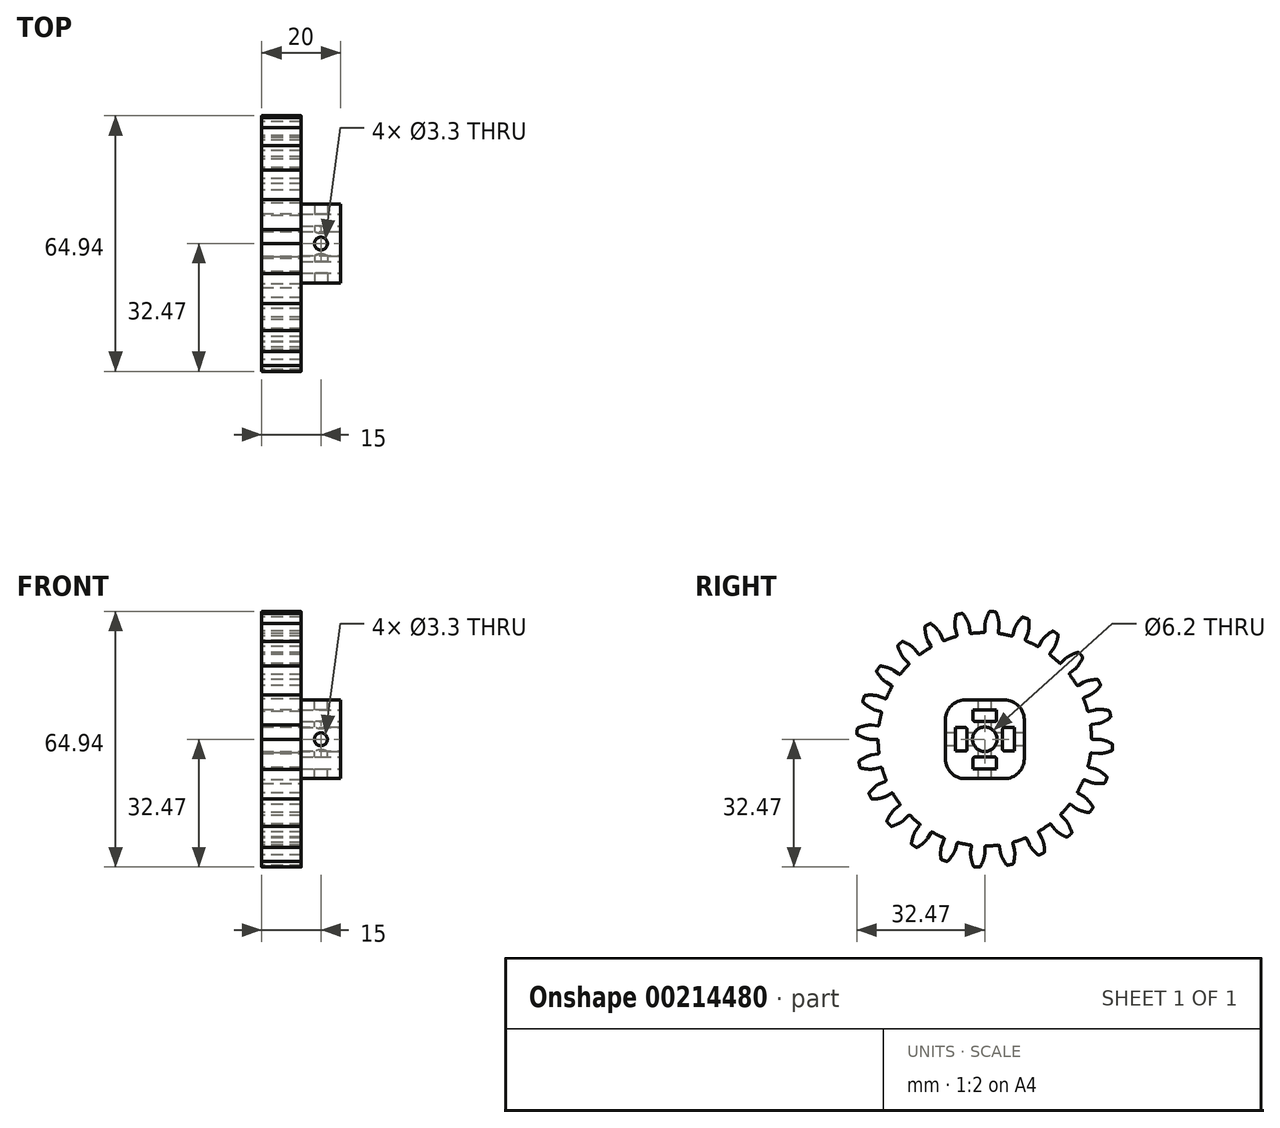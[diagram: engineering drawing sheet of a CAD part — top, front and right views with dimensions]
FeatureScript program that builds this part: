
annotation { "Feature Type Name" : "Feature", "Feature Type Description" : "" }
export const myFeature = defineFeature(function(context is Context, id is Id, definition is map)
    precondition{}
    {
        {
            assignVariable(context, id + "F0", {"name" : "NumberTeeth", "anyValue" : 24});
        }
        {
            assignVariable(context, id + "F1", {"name" : "GearThickness", "anyValue" : 10});
        }
        {
            var Q0;
            Q0=qCreatedBy(makeId("Right.planeOp"),FACE);
            var sketch = newSketch(context, id + "F2", { "sketchPlane" : qUnion([Q0])});
            skCircle(sketch, "E0", {"center": v(0, 0) * mm, "radius": 27.1 * mm});
            skCircle(sketch, "E1", {"center": v(0, 0) * mm, "radius": 29.04 * mm, "construction": true});
            skCircle(sketch, "E2", {"center": v(0, 0) * mm, "radius": 30 * mm, "construction": true});
            skCircle(sketch, "E3", {"center": v(0, 0) * mm, "radius": 32.5 * mm});
            skLineSegment(sketch, "E4", {"start": v(0, 0) * mm, "end": v(-29.04, 0) * mm, "construction": true});
            skLineSegment(sketch, "E5.1.0", {"start": v(0, 0) * mm, "end": v(-29, 1.45) * mm, "construction": true});
            skLineSegment(sketch, "E5.2.0", {"start": v(0, 0) * mm, "end": v(-28.9, 2.9) * mm, "construction": true});
            skLineSegment(sketch, "E5.3.0", {"start": v(0, 0) * mm, "end": v(-28.72, 4.34) * mm, "construction": true});
            skLineSegment(sketch, "E5.4.0", {"start": v(0, 0) * mm, "end": v(-28.47, 5.77) * mm, "construction": true});
            skLineSegment(sketch, "E5.5.0", {"start": v(0, 0) * mm, "end": v(-28.14, 7.19) * mm, "construction": true});
            skLineSegment(sketch, "E5.6.0", {"start": v(0, 0) * mm, "end": v(-27.75, 8.58) * mm, "construction": true});
            skLineSegment(sketch, "E5.7.0", {"start": v(0, 0) * mm, "end": v(-27.28, 9.96) * mm, "construction": true});
            skLineSegment(sketch, "E5.8.0", {"start": v(0, 0) * mm, "end": v(-26.75, 11.31) * mm, "construction": true});
            skLineSegment(sketch, "E5.9.0", {"start": v(0, 0) * mm, "end": v(-26.15, 12.63) * mm, "construction": true});
            skLineSegment(sketch, "E5.10.0", {"start": v(0, 0) * mm, "end": v(-25.49, 13.92) * mm, "construction": true});
            skLineSegment(sketch, "E5.11.0", {"start": v(0, 0) * mm, "end": v(-24.76, 15.18) * mm, "construction": true});
            skLineSegment(sketch, "E5.12.0", {"start": v(0, 0) * mm, "end": v(-23.97, 16.4) * mm, "construction": true});
            skLineSegment(sketch, "E5.13.0", {"start": v(0, 0) * mm, "end": v(-23.12, 17.58) * mm, "construction": true});
            skLineSegment(sketch, "E5.14.0", {"start": v(0, 0) * mm, "end": v(-22.21, 18.71) * mm, "construction": true});
            skLineSegment(sketch, "E5.anchor2", {"start": v(0, 0) * mm, "end": v(-22.21, 18.71) * mm, "construction": true});
            skLineSegment(sketch, "E6", {"start": v(-29, 1.45) * mm, "end": v(-29.08, 0) * mm, "construction": true});
            skLineSegment(sketch, "E7", {"start": v(-28.9, 2.9) * mm, "end": v(-29.19, 0) * mm, "construction": true});
            skLineSegment(sketch, "E8", {"start": v(-28.72, 4.34) * mm, "end": v(-29.37, 0.03) * mm, "construction": true});
            skLineSegment(sketch, "E9", {"start": v(-28.14, 7.19) * mm, "end": v(-29.94, 0.15) * mm, "construction": true});
            skLineSegment(sketch, "E10", {"start": v(-27.75, 8.58) * mm, "end": v(-30.32, 0.26) * mm, "construction": true});
            skLineSegment(sketch, "E11", {"start": v(-27.28, 9.96) * mm, "end": v(-30.77, 0.41) * mm, "construction": true});
            skLineSegment(sketch, "E12", {"start": v(-26.75, 11.31) * mm, "end": v(-31.28, 0.6) * mm, "construction": true});
            skLineSegment(sketch, "E13", {"start": v(-26.15, 12.63) * mm, "end": v(-31.84, 0.86) * mm, "construction": true});
            skLineSegment(sketch, "E14", {"start": v(-25.49, 13.92) * mm, "end": v(-32.45, 1.18) * mm, "construction": true});
            skLineSegment(sketch, "E15", {"start": v(-24.76, 15.18) * mm, "end": v(-33.11, 1.56) * mm, "construction": true});
            skLineSegment(sketch, "E16", {"start": v(-28.47, 5.77) * mm, "end": v(-29.62, 0.08) * mm, "construction": true});
            skLineSegment(sketch, "E17", {"start": v(-23.97, 16.4) * mm, "end": v(-33.81, 2.02) * mm, "construction": true});
            skLineSegment(sketch, "E18", {"start": v(-23.12, 17.58) * mm, "end": v(-34.55, 2.55) * mm, "construction": true});
            skLineSegment(sketch, "E19", {"start": v(-22.21, 18.71) * mm, "end": v(-35.31, 3.16) * mm, "construction": true});
            skLineSegment(sketch, "E20", {"start": v(0, 0) * mm, "end": v(-28.99, 1.8) * mm, "construction": true});
            skLineSegment(sketch, "E21", {"start": v(-27.1, 0) * mm, "end": v(-29.04, 0) * mm});
            skLineSegment(sketch, "E22.MirrorCS", {"start": v(-26.9, 3.37) * mm, "end": v(-28.82, 3.61) * mm});
            skLineSegment(sketch, "E23", {"start": v(-29.3, -1.9) * mm, "end": v(-35.31, 3.16) * mm, "construction": true});
            skFitSpline(sketch, "E24", {"points": [v(-35.31, 3.16) * mm, v(-34.55, 2.55) * mm, v(-33.81, 2.02) * mm, v(-33.11, 1.56) * mm, v(-32.45, 1.18) * mm, v(-31.84, 0.86) * mm, v(-31.28, 0.6) * mm, v(-30.77, 0.41) * mm, v(-30.32, 0.26) * mm, v(-29.94, 0.15) * mm, v(-29.62, 0.08) * mm, v(-29.37, 0.03) * mm, v(-29.19, 0) * mm, v(-29.08, 0) * mm, v(-29.04, 0) * mm], "startDerivative": vector(7.75, -6.31) * mm, "endDerivative": vector(1.01, 0) * mm});
            skFitSpline(sketch, "E25.MirrorCS", {"points": [v(-35.43, 1.25) * mm, v(-34.6, 1.77) * mm, v(-33.8, 2.2) * mm, v(-33.05, 2.57) * mm, v(-32.35, 2.86) * mm, v(-31.7, 3.1) * mm, v(-31.1, 3.28) * mm, v(-30.58, 3.42) * mm, v(-30.12, 3.51) * mm, v(-29.72, 3.57) * mm, v(-29.4, 3.6) * mm, v(-29.15, 3.62) * mm, v(-28.96, 3.62) * mm, v(-28.86, 3.61) * mm, v(-28.82, 3.61) * mm], "startDerivative": vector(8.48, 5.3) * mm, "endDerivative": vector(1, -0.13) * mm});
            skSolve(sketch);
        }
        {
            var Q0;
            {var subQ0=sQuery(id+"F2.wireOp",EDGE,"E0");var subQ27=makeQuery(id+"F2.imprint","INTERSECT",VERTEX,{"derivedFrom":[subQ0,sQuery(id+"F2.wireOp",EDGE,"10ea1024-8cf5-41f5-a75f-a634b86921f3.10.0")]});Q0=makeQuery(id+"F2.imprint","IMPRINT",FACE,{"disambiguationData":[TD([[makeQuery(id+"F2.imprint","IMPRINT",EDGE,{"disambiguationData":[TD([[subQ27,-1.0]])],"derivedFrom":subQ0}),1.0]])]});}
            var Q1;
            {var subQ0=sQuery(id+"F2.wireOp",EDGE,"10ea1024-8cf5-41f5-a75f-a634b86921f3.1.0");Q1=makeQuery(id+"F2.imprint","IMPRINT",FACE,{"disambiguationData":[TD([[makeQuery(id+"F2.imprint","IMPRINT",EDGE,{"derivedFrom":subQ0}),-1.0]])]});}
            var Q2;
            {var subQ7=sQuery(id+"F2.wireOp",EDGE,"10ea1024-8cf5-41f5-a75f-a634b86921f3.2.0");Q2=makeQuery(id+"F2.imprint","IMPRINT",FACE,{"disambiguationData":[TD([[makeQuery(id+"F2.imprint","IMPRINT",EDGE,{"derivedFrom":subQ7}),-1.0]])]});}
            var Q3;
            {var subQ8=sQuery(id+"F2.wireOp",EDGE,"10ea1024-8cf5-41f5-a75f-a634b86921f3.3.0");Q3=makeQuery(id+"F2.imprint","IMPRINT",FACE,{"disambiguationData":[TD([[makeQuery(id+"F2.imprint","IMPRINT",EDGE,{"derivedFrom":subQ8}),-1.0]])]});}
            var Q4;
            {var subQ2=sQuery(id+"F2.wireOp",EDGE,"10ea1024-8cf5-41f5-a75f-a634b86921f3.4.0");Q4=makeQuery(id+"F2.imprint","IMPRINT",FACE,{"disambiguationData":[TD([[makeQuery(id+"F2.imprint","IMPRINT",EDGE,{"derivedFrom":subQ2}),-1.0]])]});}
            var Q5;
            {var subQ8=sQuery(id+"F2.wireOp",EDGE,"10ea1024-8cf5-41f5-a75f-a634b86921f3.5.0");Q5=makeQuery(id+"F2.imprint","IMPRINT",FACE,{"disambiguationData":[TD([[makeQuery(id+"F2.imprint","IMPRINT",EDGE,{"derivedFrom":subQ8}),-1.0]])]});}
            var Q6;
            {var subQ3=sQuery(id+"F2.wireOp",EDGE,"10ea1024-8cf5-41f5-a75f-a634b86921f3.6.0");Q6=makeQuery(id+"F2.imprint","IMPRINT",FACE,{"disambiguationData":[TD([[makeQuery(id+"F2.imprint","IMPRINT",EDGE,{"derivedFrom":subQ3}),-1.0]])]});}
            var Q7;
            {var subQ0=sQuery(id+"F2.wireOp",EDGE,"10ea1024-8cf5-41f5-a75f-a634b86921f3.7.0");Q7=makeQuery(id+"F2.imprint","IMPRINT",FACE,{"disambiguationData":[TD([[makeQuery(id+"F2.imprint","IMPRINT",EDGE,{"derivedFrom":subQ0}),-1.0]])]});}
            var Q8;
            {var subQ5=sQuery(id+"F2.wireOp",EDGE,"10ea1024-8cf5-41f5-a75f-a634b86921f3.8.0");Q8=makeQuery(id+"F2.imprint","IMPRINT",FACE,{"disambiguationData":[TD([[makeQuery(id+"F2.imprint","IMPRINT",EDGE,{"derivedFrom":subQ5}),-1.0]])]});}
            var Q9;
            {var subQ1=sQuery(id+"F2.wireOp",EDGE,"10ea1024-8cf5-41f5-a75f-a634b86921f3.9.0");Q9=makeQuery(id+"F2.imprint","IMPRINT",FACE,{"disambiguationData":[TD([[makeQuery(id+"F2.imprint","IMPRINT",EDGE,{"derivedFrom":subQ1}),-1.0]])]});}
            var Q10;
            {var subQ5=sQuery(id+"F2.wireOp",EDGE,"10ea1024-8cf5-41f5-a75f-a634b86921f3.10.0");Q10=makeQuery(id+"F2.imprint","IMPRINT",FACE,{"disambiguationData":[TD([[makeQuery(id+"F2.imprint","IMPRINT",EDGE,{"derivedFrom":subQ5}),-1.0]])]});}
            var Q11;
            {var subQ8=sQuery(id+"F2.wireOp",EDGE,"10ea1024-8cf5-41f5-a75f-a634b86921f3.11.0");Q11=makeQuery(id+"F2.imprint","IMPRINT",FACE,{"disambiguationData":[TD([[makeQuery(id+"F2.imprint","IMPRINT",EDGE,{"derivedFrom":subQ8}),-1.0]])]});}
            var Q12;
            {var subQ2=sQuery(id+"F2.wireOp",EDGE,"10ea1024-8cf5-41f5-a75f-a634b86921f3.12.0");Q12=makeQuery(id+"F2.imprint","IMPRINT",FACE,{"disambiguationData":[TD([[makeQuery(id+"F2.imprint","IMPRINT",EDGE,{"derivedFrom":subQ2}),-1.0]])]});}
            var Q13;
            {var subQ3=sQuery(id+"F2.wireOp",EDGE,"10ea1024-8cf5-41f5-a75f-a634b86921f3.13.0");Q13=makeQuery(id+"F2.imprint","IMPRINT",FACE,{"disambiguationData":[TD([[makeQuery(id+"F2.imprint","IMPRINT",EDGE,{"derivedFrom":subQ3}),-1.0]])]});}
            var Q14;
            {var subQ0=sQuery(id+"F2.wireOp",EDGE,"10ea1024-8cf5-41f5-a75f-a634b86921f3.14.0");Q14=makeQuery(id+"F2.imprint","IMPRINT",FACE,{"disambiguationData":[TD([[makeQuery(id+"F2.imprint","IMPRINT",EDGE,{"derivedFrom":subQ0}),-1.0]])]});}
            var Q15;
            {var subQ6=sQuery(id+"F2.wireOp",EDGE,"10ea1024-8cf5-41f5-a75f-a634b86921f3.15.0");Q15=makeQuery(id+"F2.imprint","IMPRINT",FACE,{"disambiguationData":[TD([[makeQuery(id+"F2.imprint","IMPRINT",EDGE,{"derivedFrom":subQ6}),-1.0]])]});}
            var Q16;
            {var subQ5=sQuery(id+"F2.wireOp",EDGE,"10ea1024-8cf5-41f5-a75f-a634b86921f3.16.0");Q16=makeQuery(id+"F2.imprint","IMPRINT",FACE,{"disambiguationData":[TD([[makeQuery(id+"F2.imprint","IMPRINT",EDGE,{"derivedFrom":subQ5}),-1.0]])]});}
            var Q17;
            {var subQ7=sQuery(id+"F2.wireOp",EDGE,"10ea1024-8cf5-41f5-a75f-a634b86921f3.17.0");Q17=makeQuery(id+"F2.imprint","IMPRINT",FACE,{"disambiguationData":[TD([[makeQuery(id+"F2.imprint","IMPRINT",EDGE,{"derivedFrom":subQ7}),-1.0]])]});}
            var Q18;
            {var subQ5=sQuery(id+"F2.wireOp",EDGE,"10ea1024-8cf5-41f5-a75f-a634b86921f3.18.0");Q18=makeQuery(id+"F2.imprint","IMPRINT",FACE,{"disambiguationData":[TD([[makeQuery(id+"F2.imprint","IMPRINT",EDGE,{"derivedFrom":subQ5}),-1.0]])]});}
            var Q19;
            {var subQ8=sQuery(id+"F2.wireOp",EDGE,"10ea1024-8cf5-41f5-a75f-a634b86921f3.19.0");Q19=makeQuery(id+"F2.imprint","IMPRINT",FACE,{"disambiguationData":[TD([[makeQuery(id+"F2.imprint","IMPRINT",EDGE,{"derivedFrom":subQ8}),-1.0]])]});}
            var Q20;
            {var subQ8=sQuery(id+"F2.wireOp",EDGE,"E21");Q20=makeQuery(id+"F2.imprint","IMPRINT",FACE,{"disambiguationData":[TD([[makeQuery(id+"F2.imprint","IMPRINT",EDGE,{"derivedFrom":subQ8}),-1.0]])]});}
            extrude(context, id + "F3", {"entities" : qUnion([Q0, Q1, Q2, Q3, Q4, Q5, Q6, Q7, Q8, Q9, Q10, Q11, Q12, Q13, Q14, Q15, Q16, Q17, Q18, Q19, Q20]), "depth" : (getVariable(context, 'GearThickness')) * mm});
        }
        {
            var Q0;
            Q0=makeQuery(id+"F3.opExtrude","SWEPT_EDGE",EDGE,{"disambiguationData":[OSD([sQuery(id+"F2.wireOp",EDGE,"E0"),sQuery(id+"F2.wireOp",EDGE,"E22.MirrorCS")])]});
            var Q1;
            Q1=makeQuery(id+"F3.opExtrude","SWEPT_EDGE",EDGE,{"disambiguationData":[OSD([sQuery(id+"F2.wireOp",EDGE,"E3"),sQuery(id+"F2.wireOp",EDGE,"E25.MirrorCS")])]});
            var Q2;
            Q2=makeQuery(id+"F3.opExtrude","SWEPT_EDGE",EDGE,{"disambiguationData":[OSD([sQuery(id+"F2.wireOp",EDGE,"E3"),sQuery(id+"F2.wireOp",EDGE,"E24")])]});
            var Q3;
            Q3=makeQuery(id+"F3.opExtrude","SWEPT_EDGE",EDGE,{"disambiguationData":[OSD([sQuery(id+"F2.wireOp",EDGE,"E0"),sQuery(id+"F2.wireOp",EDGE,"E21")])]});
            fillet(context, id + "F4", {"entities" : qUnion([Q0, Q1, Q2, Q3]), "radius" : 0.3 * mm, "tangentPropagation" : true, "allowEdgeOverflow" : false});
        }
        {
            var Q0;
            Q0=makeQuery(id+"F3.opExtrude","SWEPT_FACE",FACE,{"disambiguationData":[OSD([sQuery(id+"F2.wireOp",EDGE,"E22.MirrorCS")])]});
            var Q1;
            Q1=makeQuery(id+"F3.opExtrude","SWEPT_FACE",FACE,{"disambiguationData":[OSD([sQuery(id+"F2.wireOp",EDGE,"E25.MirrorCS")])]});
            var Q2;
            Q2=makeQuery(id+"F3.opExtrude","SWEPT_FACE",FACE,{"disambiguationData":[OSD([sQuery(id+"F2.wireOp",EDGE,"E3")])]});
            var Q3;
            Q3=makeQuery(id+"F3.opExtrude","SWEPT_FACE",FACE,{"disambiguationData":[OSD([sQuery(id+"F2.wireOp",EDGE,"E24")])]});
            var Q4;
            Q4=makeQuery(id+"F3.opExtrude","SWEPT_FACE",FACE,{"disambiguationData":[OSD([sQuery(id+"F2.wireOp",EDGE,"E21")])]});
            var Q5;
            Q5=makeQuery(id+"F4.opFillet","BLEND_FACE",FACE,{"disambiguationData":[OSD([sQuery(id+"F2.wireOp",EDGE,"E0"),sQuery(id+"F2.wireOp",EDGE,"E22.MirrorCS")])]});
            var Q6;
            Q6=makeQuery(id+"F4.opFillet","BLEND_FACE",FACE,{"disambiguationData":[OSD([sQuery(id+"F2.wireOp",EDGE,"E3"),sQuery(id+"F2.wireOp",EDGE,"E25.MirrorCS")])]});
            var Q7;
            Q7=makeQuery(id+"F4.opFillet","BLEND_FACE",FACE,{"disambiguationData":[OSD([sQuery(id+"F2.wireOp",EDGE,"E3"),sQuery(id+"F2.wireOp",EDGE,"E24")])]});
            var Q8;
            Q8=makeQuery(id+"F4.opFillet","BLEND_FACE",FACE,{"disambiguationData":[OSD([sQuery(id+"F2.wireOp",EDGE,"E0"),sQuery(id+"F2.wireOp",EDGE,"E21")])]});
            var Q9;
            Q9=makeQuery(id+"F3.opExtrude","SWEPT_FACE",FACE,{"disambiguationData":[OSD([sQuery(id+"F2.wireOp",EDGE,"E0")])]});
            circularPattern(context, id + "F5", {"faces" : qUnion([Q0, Q1, Q2, Q3, Q4, Q5, Q6, Q7, Q8]), "axis" : qUnion([Q9]), "angle" : 360 * degree, "instanceCount" : getVariable(context, 'NumberTeeth'), "equalSpace" : true, "patternType" : PatternType.FACE});
        }
        {
            var Q0;
            Q0=makeQuery(id+"F3.opExtrude","CAP_FACE",FACE,{"disambiguationData":[OSD([sQuery(id+"F2.wireOp",EDGE,"E0"),sQuery(id+"F2.wireOp",EDGE,"E3"),sQuery(id+"F2.wireOp",EDGE,"E21"),sQuery(id+"F2.wireOp",EDGE,"E22.MirrorCS"),sQuery(id+"F2.wireOp",EDGE,"E24"),sQuery(id+"F2.wireOp",EDGE,"E25.MirrorCS")])],"isStart":false});
            var sketch = newSketch(context, id + "F6", { "sketchPlane" : qUnion([Q0])});
            skLineSegment(sketch, "E26.bottom", {"start": v(10, 10) * mm, "end": v(-10, 10) * mm});
            skLineSegment(sketch, "E26.top", {"start": v(10, -10) * mm, "end": v(-10, -10) * mm});
            skLineSegment(sketch, "E26.left", {"start": v(10, 10) * mm, "end": v(10, -10) * mm});
            skLineSegment(sketch, "E26.right", {"start": v(-10, 10) * mm, "end": v(-10, -10) * mm});
            skPoint(sketch, "E26.middle", {"position": v(0, 0) * mm});
            skSolve(sketch);
        }
        {
            var Q0;
            Q0=makeQuery(id+"F6.imprint","IMPRINT",FACE,{"disambiguationData":[TD([[makeQuery(id+"F6.imprint","IMPRINT",EDGE,{"derivedFrom":sQuery(id+"F6.wireOp",EDGE,"E26.bottom")}),1.0]])]});
            extrude(context, id + "F7", {"entities" : qUnion([Q0]), "operationType" : NewBodyOperationType.ADD, "depth" : 10 * mm});
        }
        {
            var Q0;
            Q0=makeQuery(id+"F7.opExtrude","CAP_FACE",FACE,{"disambiguationData":[OSD([sQuery(id+"F6.wireOp",EDGE,"E26.bottom"),sQuery(id+"F6.wireOp",EDGE,"E26.top"),sQuery(id+"F6.wireOp",EDGE,"E26.left"),sQuery(id+"F6.wireOp",EDGE,"E26.right")])],"isStart":false});
            var sketch = newSketch(context, id + "F8", { "sketchPlane" : qUnion([Q0])});
            skCircle(sketch, "E27", {"center": v(0, 0) * mm, "radius": 3.1 * mm});
            skLineSegment(sketch, "E28", {"start": v(0, 10) * mm, "end": v(0, -10) * mm, "construction": true});
            skLineSegment(sketch, "E29", {"start": v(10, 0) * mm, "end": v(-10, 0) * mm, "construction": true});
            skLineSegment(sketch, "E30.bottom", {"start": v(3, 7.5) * mm, "end": v(-3, 7.5) * mm});
            skLineSegment(sketch, "E30.top", {"start": v(3, 4.5) * mm, "end": v(-3, 4.5) * mm});
            skLineSegment(sketch, "E30.left", {"start": v(3, 7.5) * mm, "end": v(3, 4.5) * mm});
            skLineSegment(sketch, "E30.right", {"start": v(-3, 7.5) * mm, "end": v(-3, 4.5) * mm});
            skPoint(sketch, "E30.middle", {"position": v(0, 6) * mm});
            skLineSegment(sketch, "E31.1.0", {"start": v(-7.5, -3) * mm, "end": v(-4.5, -3) * mm});
            skLineSegment(sketch, "E31.1.1", {"start": v(-4.5, 3) * mm, "end": v(-4.5, -3) * mm});
            skLineSegment(sketch, "E31.1.2", {"start": v(-7.5, 3) * mm, "end": v(-4.5, 3) * mm});
            skLineSegment(sketch, "E31.1.3", {"start": v(-7.5, 3) * mm, "end": v(-7.5, -3) * mm});
            skLineSegment(sketch, "E31.2.0", {"start": v(3, -7.5) * mm, "end": v(3, -4.5) * mm});
            skLineSegment(sketch, "E31.2.1", {"start": v(-3, -4.5) * mm, "end": v(3, -4.5) * mm});
            skLineSegment(sketch, "E31.2.2", {"start": v(-3, -7.5) * mm, "end": v(-3, -4.5) * mm});
            skLineSegment(sketch, "E31.2.3", {"start": v(-3, -7.5) * mm, "end": v(3, -7.5) * mm});
            skLineSegment(sketch, "E31.3.0", {"start": v(7.5, 3) * mm, "end": v(4.5, 3) * mm});
            skLineSegment(sketch, "E31.3.1", {"start": v(4.5, -3) * mm, "end": v(4.5, 3) * mm});
            skLineSegment(sketch, "E31.3.2", {"start": v(7.5, -3) * mm, "end": v(4.5, -3) * mm});
            skLineSegment(sketch, "E31.3.3", {"start": v(7.5, -3) * mm, "end": v(7.5, 3) * mm});
            skSolve(sketch);
        }
        {
            var Q0;
            Q0=makeQuery(id+"F8.imprint","IMPRINT",FACE,{"disambiguationData":[TD([[makeQuery(id+"F8.imprint","IMPRINT",EDGE,{"derivedFrom":sQuery(id+"F8.wireOp",EDGE,"E27")}),1.0]])]});
            extrude(context, id + "F9", {"entities" : qUnion([Q0]), "operationType" : NewBodyOperationType.REMOVE, "endBound" : BoundingType.THROUGH_ALL, "oppositeDirection" : true, "depth" : 25 * mm});
        }
        {
            var Q0;
            Q0=makeQuery(id+"F8.imprint","IMPRINT",FACE,{"disambiguationData":[TD([[makeQuery(id+"F8.imprint","IMPRINT",EDGE,{"derivedFrom":sQuery(id+"F8.wireOp",EDGE,"E30.bottom")}),1.0]])]});
            var Q1;
            Q1=makeQuery(id+"F8.imprint","IMPRINT",FACE,{"disambiguationData":[TD([[makeQuery(id+"F8.imprint","IMPRINT",EDGE,{"derivedFrom":sQuery(id+"F8.wireOp",EDGE,"E31.3.0")}),1.0]])]});
            var Q2;
            Q2=makeQuery(id+"F8.imprint","IMPRINT",FACE,{"disambiguationData":[TD([[makeQuery(id+"F8.imprint","IMPRINT",EDGE,{"derivedFrom":sQuery(id+"F8.wireOp",EDGE,"E31.1.0")}),1.0]])]});
            var Q3;
            Q3=makeQuery(id+"F8.imprint","IMPRINT",FACE,{"disambiguationData":[TD([[makeQuery(id+"F8.imprint","IMPRINT",EDGE,{"derivedFrom":sQuery(id+"F8.wireOp",EDGE,"E31.2.0")}),1.0]])]});
            extrude(context, id + "F10", {"entities" : qUnion([Q0, Q1, Q2, Q3]), "operationType" : NewBodyOperationType.REMOVE, "oppositeDirection" : true, "depth" : 10 * mm});
        }
        {
            var Q0;
            Q0=makeQuery(id+"F7.opExtrude","SWEPT_FACE",FACE,{"disambiguationData":[OSD([sQuery(id+"F6.wireOp",EDGE,"E26.bottom")])]});
            var sketch = newSketch(context, id + "F11", { "sketchPlane" : qUnion([Q0])});
            skPoint(sketch, "E32", {"position": v(15, 0) * mm});
            skPoint(sketch, "E32.positionSnap0", {"position": v(15, 10) * mm});
            skPoint(sketch, "E32.positionSnap1", {"position": v(20, 0) * mm});
            skSolve(sketch);
        }
        {
            var Q0;
            Q0=makeQuery(id+"F7.opExtrude","SWEPT_FACE",FACE,{"disambiguationData":[OSD([sQuery(id+"F6.wireOp",EDGE,"E26.right")])]});
            var sketch = newSketch(context, id + "F12", { "sketchPlane" : qUnion([Q0])});
            skPoint(sketch, "E33", {"position": v(15, 0) * mm});
            skPoint(sketch, "E33.positionSnap0", {"position": v(15, 10) * mm});
            skPoint(sketch, "E33.positionSnap1", {"position": v(20, 0) * mm});
            skSolve(sketch);
        }
        {
            var Q0;
            Q0=sQuery(id+"F12.wireOp",VERTEX,"E33");
            var Q1;
            Q1=sQuery(id+"F11.wireOp",VERTEX,"E32");
            var Q2;
            Q2=makeQuery(id+"F3.opExtrude","SWEPT_BODY",BODY,{"disambiguationData":[OSD([sQuery(id+"F2.wireOp",EDGE,"E0"),sQuery(id+"F2.wireOp",EDGE,"E3"),sQuery(id+"F2.wireOp",EDGE,"E21"),sQuery(id+"F2.wireOp",EDGE,"E22.MirrorCS"),sQuery(id+"F2.wireOp",EDGE,"E24"),sQuery(id+"F2.wireOp",EDGE,"E25.MirrorCS")])]});
            hole(context, id + "F13", {"style" : HoleStyle.SIMPLE, "endStyle" : HoleEndStyle.THROUGH, "standardTappedOrClearance" : lookupTablePath({ "standard" : "ISO", "fit" : "Normal", "size" : "M3", "type" : "Clearance" }), "standardBlindInLast" : lookupTablePath({ "fit" : "Standard", "standard" : "ISO", "size" : "M3", "type" : "Clearance" }), "holeDiameter" : 3.3 * mm, "locations" : qUnion([Q0, Q1]), "scope" : qUnion([Q2]), "isTappedThrough" : true});
        }
        {
            var Q0;
            Q0=makeQuery(id+"F10.boolean.opBoolean","COPY",EDGE,{"derivedFrom":makeQuery(id+"F10.opExtrude","SWEPT_EDGE",EDGE,{"disambiguationData":[OSD([sQuery(id+"F8.wireOp",EDGE,"E30.top"),sQuery(id+"F8.wireOp",EDGE,"E30.left")])]})});
            var Q1;
            Q1=makeQuery(id+"F10.boolean.opBoolean","COPY",EDGE,{"derivedFrom":makeQuery(id+"F10.opExtrude","SWEPT_EDGE",EDGE,{"disambiguationData":[OSD([sQuery(id+"F8.wireOp",EDGE,"E30.top"),sQuery(id+"F8.wireOp",EDGE,"E30.right")])]})});
            var Q2;
            Q2=makeQuery(id+"F10.boolean.opBoolean","COPY",EDGE,{"derivedFrom":makeQuery(id+"F10.opExtrude","SWEPT_EDGE",EDGE,{"disambiguationData":[OSD([sQuery(id+"F8.wireOp",EDGE,"E31.1.0"),sQuery(id+"F8.wireOp",EDGE,"E31.1.1")])]})});
            var Q3;
            Q3=makeQuery(id+"F10.boolean.opBoolean","COPY",EDGE,{"derivedFrom":makeQuery(id+"F10.opExtrude","SWEPT_EDGE",EDGE,{"disambiguationData":[OSD([sQuery(id+"F8.wireOp",EDGE,"E31.1.1"),sQuery(id+"F8.wireOp",EDGE,"E31.1.2")])]})});
            var Q4;
            Q4=makeQuery(id+"F10.boolean.opBoolean","COPY",EDGE,{"derivedFrom":makeQuery(id+"F10.opExtrude","SWEPT_EDGE",EDGE,{"disambiguationData":[OSD([sQuery(id+"F8.wireOp",EDGE,"E31.2.1"),sQuery(id+"F8.wireOp",EDGE,"E31.2.2")])]})});
            var Q5;
            Q5=makeQuery(id+"F10.boolean.opBoolean","COPY",EDGE,{"derivedFrom":makeQuery(id+"F10.opExtrude","SWEPT_EDGE",EDGE,{"disambiguationData":[OSD([sQuery(id+"F8.wireOp",EDGE,"E31.2.0"),sQuery(id+"F8.wireOp",EDGE,"E31.2.1")])]})});
            var Q6;
            Q6=makeQuery(id+"F10.boolean.opBoolean","COPY",EDGE,{"derivedFrom":makeQuery(id+"F10.opExtrude","SWEPT_EDGE",EDGE,{"disambiguationData":[OSD([sQuery(id+"F8.wireOp",EDGE,"E31.3.1"),sQuery(id+"F8.wireOp",EDGE,"E31.3.2")])]})});
            var Q7;
            Q7=makeQuery(id+"F10.boolean.opBoolean","COPY",EDGE,{"derivedFrom":makeQuery(id+"F10.opExtrude","SWEPT_EDGE",EDGE,{"disambiguationData":[OSD([sQuery(id+"F8.wireOp",EDGE,"E31.3.0"),sQuery(id+"F8.wireOp",EDGE,"E31.3.1")])]})});
            fillet(context, id + "F14", {"entities" : qUnion([Q0, Q1, Q2, Q3, Q4, Q5, Q6, Q7]), "radius" : 0.5 * mm, "tangentPropagation" : true, "allowEdgeOverflow" : false});
        }
        {
            var Q0;
            Q0=makeQuery(id+"F7.opExtrude","SWEPT_EDGE",EDGE,{"disambiguationData":[OSD([sQuery(id+"F6.wireOp",EDGE,"E26.bottom"),sQuery(id+"F6.wireOp",EDGE,"E26.left")])]});
            var Q1;
            Q1=makeQuery(id+"F7.opExtrude","SWEPT_EDGE",EDGE,{"disambiguationData":[OSD([sQuery(id+"F6.wireOp",EDGE,"E26.top"),sQuery(id+"F6.wireOp",EDGE,"E26.left")])]});
            var Q2;
            Q2=makeQuery(id+"F7.opExtrude","SWEPT_EDGE",EDGE,{"disambiguationData":[OSD([sQuery(id+"F6.wireOp",EDGE,"E26.top"),sQuery(id+"F6.wireOp",EDGE,"E26.right")])]});
            var Q3;
            Q3=makeQuery(id+"F7.opExtrude","SWEPT_EDGE",EDGE,{"disambiguationData":[OSD([sQuery(id+"F6.wireOp",EDGE,"E26.bottom"),sQuery(id+"F6.wireOp",EDGE,"E26.right")])]});
            fillet(context, id + "F15", {"entities" : qUnion([Q0, Q1, Q2, Q3]), "radius" : 5 * mm, "tangentPropagation" : true, "allowEdgeOverflow" : false});
        }
    });
